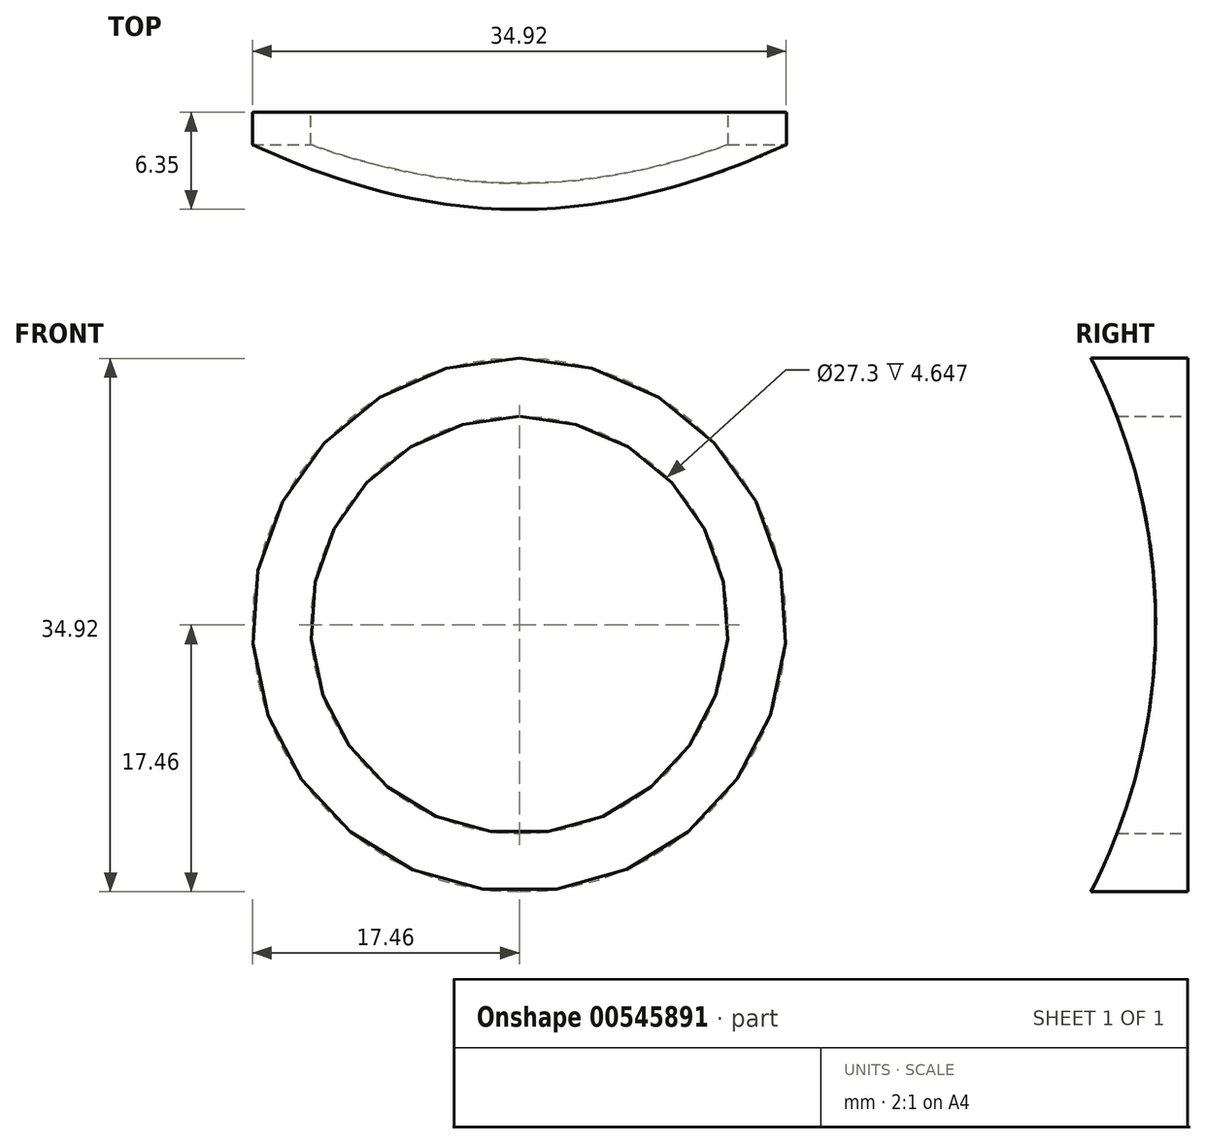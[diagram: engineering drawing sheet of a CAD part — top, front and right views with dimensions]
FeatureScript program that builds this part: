
annotation { "Feature Type Name" : "Feature", "Feature Type Description" : "" }
export const myFeature = defineFeature(function(context is Context, id is Id, definition is map)
    precondition{}
    {
        {
            var Q0;
            Q0=qCreatedBy(makeId("Front.planeOp"),FACE);
            var sketch = newSketch(context, id + "F0", { "sketchPlane" : qUnion([Q0])});
            skCircle(sketch, "E0", {"center": v(0, 0) * mm, "radius": 17.46 * mm});
            skCircle(sketch, "E1", {"center": v(0, 0) * mm, "radius": 13.65 * mm});
            skSolve(sketch);
        }
        {
            var Q0;
            Q0 = qSketchRegion(id + "F0", true);
            extrude(context, id + "F1", {"entities" : qUnion([Q0]), "depth" : 6.35 * mm, "offsetDistance" : 25.4 * mm});
        }
        {
            var Q0;
            Q0=qCreatedBy(makeId("Right.planeOp"),FACE);
            var sketch = newSketch(context, id + "F2", { "sketchPlane" : qUnion([Q0])});
            skLineSegment(sketch, "E2.0", {"start": v(-6.35, -17.46) * mm, "end": v(-6.35, 17.46) * mm, "construction": true});
            skArc(sketch, "E3", {"start": v(-6.35, -17.46) * mm, "mid": v(-2.11, 0) * mm, "end": v(-6.35, 17.46) * mm});
            skLineSegment(sketch, "E4", {"start": v(-6.35, 17.46) * mm, "end": v(-6.35, -17.46) * mm});
            skSolve(sketch);
        }
        {
            var Q0;
            Q0 = qSketchRegion(id + "F2", true);
            extrude(context, id + "F3", {"entities" : qUnion([Q0]), "operationType" : NewBodyOperationType.REMOVE, "endBound" : BoundingType.THROUGH_ALL, "oppositeDirection" : true, "depth" : 25.4 * mm, "offsetDistance" : 25.4 * mm, "hasSecondDirection" : true, "secondDirectionBound" : SecondDirectionBoundingType.THROUGH_ALL, "secondDirectionOppositeDirection" : false, "secondDirectionDepth" : 25.4 * mm});
        }
    });
